# Revit family: Leitungsmaterial_Rundleiter_Edelstahl
name_source: partatom
category: Generic Models
revit_build: Autodesk Revit 2015 (Build: 20140606_1530(x64)
units: mm (PartAtom-declared; Revit-internal decimal feet)

## types (7) — shared parameters
Manufacturer = OBO Bettermann
Material = Stainless Steel AISI 304
URL = http://www.obo-bettermann.com

## per-type parameters (varying)
| type | Article Type | Diameter dimesion | GTIN | Manufacturer Art. No. |
| RD 8-V2A | RD 8-V2A | 8 mm  [stored 0.0262467 ft] | 4012195680529 | 5021235 |
| RD10-V2A(2) | RD 10-V2A | 10 mm  [stored 0.0328084 ft] | 4012195680567 | 5021239 |
| RD 8-V4A | RD 8-V4A | 8 mm  [stored 0.0262467 ft] | 4012195680574 | 5021644 |
| RD 10-V2A | RD 10-V2A | 10 mm  [stored 0.0328084 ft] | 4012195801375 | 5021227 |
| RD 10-V4A 20 | RD 10-V4A 20 | 10 mm  [stored 0.0328084 ft] | 4012196282425 | 5021640 |
| RD 10-V4A | RD 10-V4A | 10 mm  [stored 0.0328084 ft] | 4012195902058 | 5021642 |
| RD 10-V4A(2) | RD 10-V4A | 10 mm  [stored 0.0328084 ft] | 4012195680581 | 5021647 |

note: [stored X ft] marks values corroborated as IEEE doubles in the binary element streams (Revit-internal decimal feet)

## geometry (parser evidence)
native form markers: Sweep x2
no freeform markers — native parametric forms only
